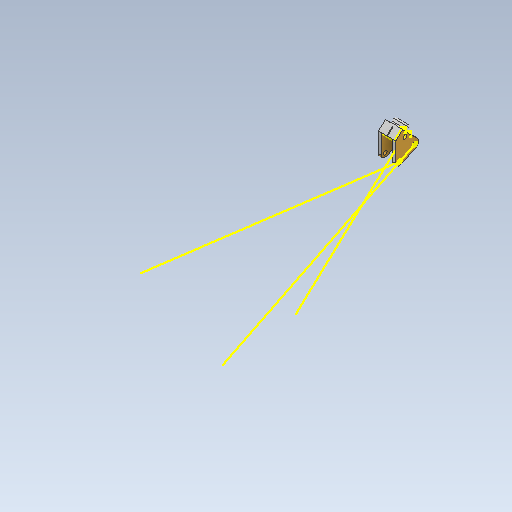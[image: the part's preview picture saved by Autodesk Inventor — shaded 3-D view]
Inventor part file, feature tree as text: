
AUTODESK INVENTOR PART (.ipt)
format: ipt  version: 2020 (Build 240168000, 168)  size: 323,584 bytes
history: native  units: mm
features: sketch x8, other x4, projected_geometry x4, extrude x3
ambient origin geometry x8: Origin, YZ Plane, XZ Plane, XY Plane, X Axis, Y Axis, Z Axis, Center Point
bodies: Solid2 (feature_tree)
feature tree (19):
  other  "preadator nano fixed mount template.iam"
  other  "Kauri modular camera mount HDzero micro v1 mirror.ipt:1"
  other  "Kauri modular camera mount HDzero micro v1.ipt:1"
  other  "camera housing V1.ipt:1"
  extrude  "Extrusion1"  Depth=10.0mm TaperAngle=0.0deg
  extrude  "Extrusion2"  Depth=0.5mm
  extrude  "Extrusion3"  Depth=10.0mm TaperAngle=0.0deg
  sketch  "Sketch1"  dims[d1=10.0mm d2=10.0mm d3=0.0mm]
  sketch  "Sketch1_1"  dims[d4=10.0mm d5=0.0mm d6=0.5mm]
  sketch  "Sketch6"
  sketch  "Sketch11"
  sketch  "Sketch10"
  projected_geometry  "Projected Loop3"
  sketch  "Sketch12"
  projected_geometry  "Projected Loop4"
  projected_geometry  "Projected Loop5"
  sketch  "Sketch13"
  projected_geometry  "Projected Loop6"
  sketch  "Sketch10_1"  dims[d7=0.5mm d8=10.0mm d9=0.0mm]
